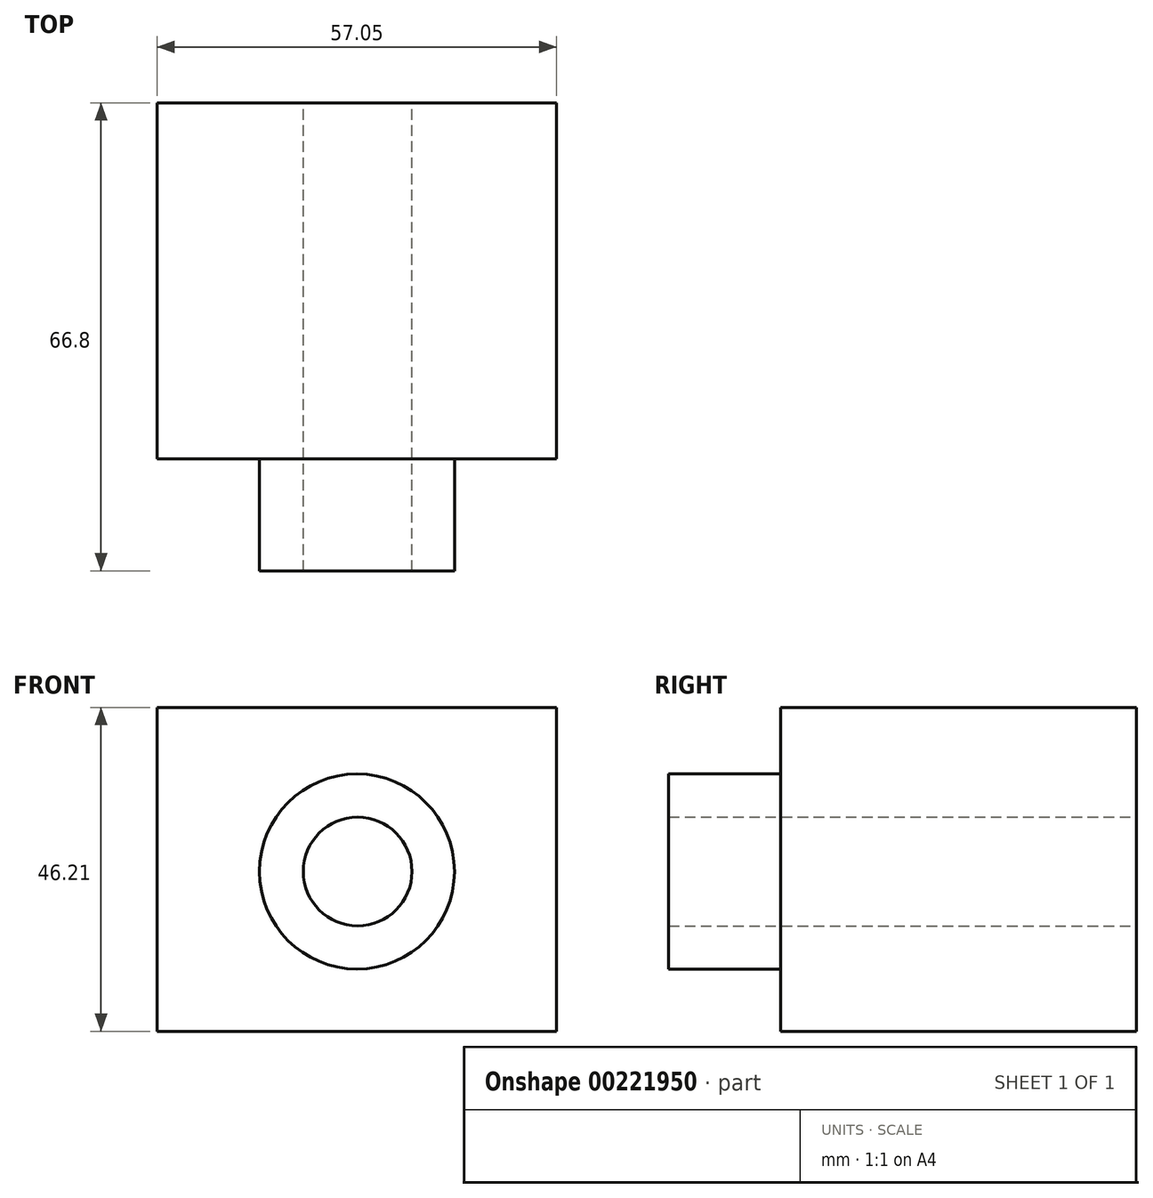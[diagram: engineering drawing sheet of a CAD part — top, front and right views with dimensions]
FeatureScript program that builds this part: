
annotation { "Feature Type Name" : "Feature", "Feature Type Description" : "" }
export const myFeature = defineFeature(function(context is Context, id is Id, definition is map)
    precondition{}
    {
        {
            var Q0;
            Q0=qCreatedBy(makeId("Front.planeOp"),FACE);
            var sketch = newSketch(context, id + "F0", { "sketchPlane" : qUnion([Q0])});
            skLineSegment(sketch, "E0.bottom", {"start": v(-15.22, 5) * mm, "end": v(-72.27, 5) * mm});
            skLineSegment(sketch, "E0.top", {"start": v(-15.22, 51.22) * mm, "end": v(-72.27, 51.22) * mm});
            skLineSegment(sketch, "E0.left", {"start": v(-15.22, 5) * mm, "end": v(-15.22, 51.22) * mm});
            skLineSegment(sketch, "E0.right", {"start": v(-72.27, 5) * mm, "end": v(-72.27, 51.22) * mm});
            skPoint(sketch, "E0.middle", {"position": v(-43.75, 28.11) * mm});
            skSolve(sketch);
        }
        {
            var Q0;
            Q0 = qSketchRegion(id + "F0", true);
            extrude(context, id + "F1", {"entities" : qUnion([Q0]), "depth" : 50.8 * mm});
        }
        {
            var Q0;
            Q0=qCreatedBy(makeId("Front.planeOp"),FACE);
            var sketch = newSketch(context, id + "F2", { "sketchPlane" : qUnion([Q0])});
            skCircle(sketch, "E1", {"center": v(-43.73, 27.81) * mm, "radius": 13.92 * mm});
            skSolve(sketch);
        }
        {
            var Q0;
            Q0 = qSketchRegion(id + "F2", true);
            extrude(context, id + "F3", {"entities" : qUnion([Q0]), "operationType" : NewBodyOperationType.ADD, "depth" : 66.8 * mm});
        }
        {
            var Q0;
            Q0=qCreatedBy(makeId("Front.planeOp"),FACE);
            var sketch = newSketch(context, id + "F4", { "sketchPlane" : qUnion([Q0])});
            skCircle(sketch, "E2", {"center": v(-43.64, 27.81) * mm, "radius": 7.76 * mm});
            skSolve(sketch);
        }
        {
            var Q0;
            Q0 = qSketchRegion(id + "F4", true);
            extrude(context, id + "F5", {"entities" : qUnion([Q0]), "operationType" : NewBodyOperationType.REMOVE, "endBound" : BoundingType.THROUGH_ALL, "depth" : 97.03 * mm});
        }
    });
